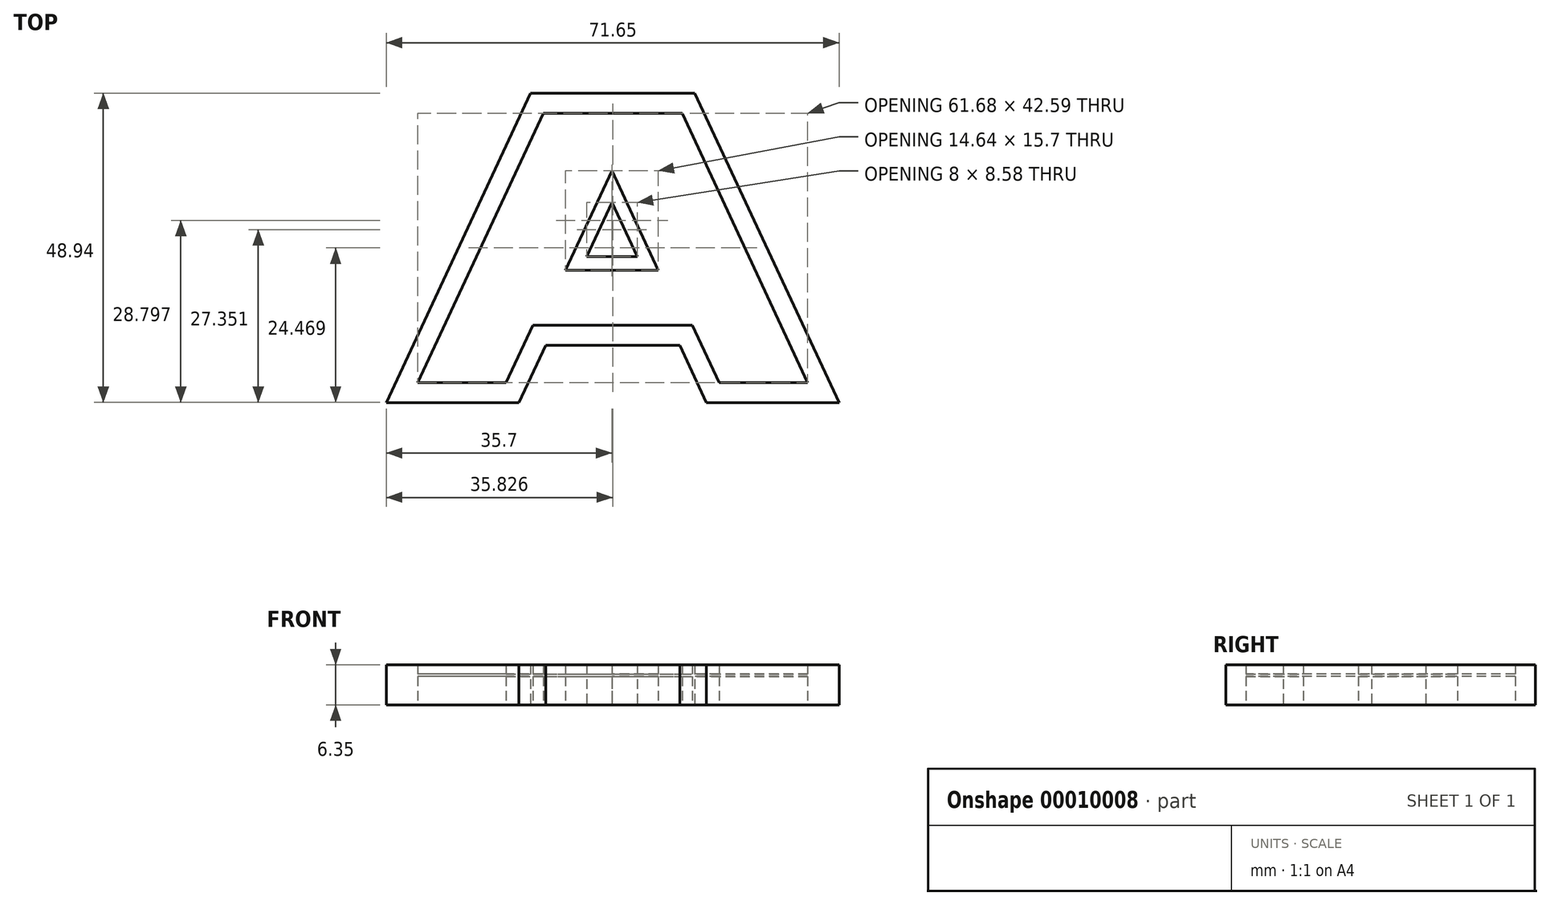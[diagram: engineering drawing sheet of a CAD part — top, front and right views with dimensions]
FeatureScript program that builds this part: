
annotation { "Feature Type Name" : "Feature", "Feature Type Description" : "" }
export const myFeature = defineFeature(function(context is Context, id is Id, definition is map)
    precondition{}
    {
        {
            var Q0;
            Q0=qCreatedBy(makeId("Top.planeOp"),FACE);
            var sketch = newSketch(context, id + "F0", { "sketchPlane" : qUnion([Q0])});
            skLineSegment(sketch, "E0", {"start": v(-12.87, 17.3) * mm, "end": v(13.13, 17.3) * mm});
            skLineSegment(sketch, "E1", {"start": v(13.13, 17.3) * mm, "end": v(35.95, -31.64) * mm});
            skLineSegment(sketch, "E2", {"start": v(-12.87, 17.3) * mm, "end": v(-35.7, -31.64) * mm});
            skLineSegment(sketch, "E3", {"start": v(-14.7, -31.64) * mm, "end": v(-35.7, -31.64) * mm});
            skLineSegment(sketch, "E4", {"start": v(35.95, -31.64) * mm, "end": v(14.95, -31.64) * mm});
            skLineSegment(sketch, "E5", {"start": v(-14.7, -31.64) * mm, "end": v(-10.47, -22.58) * mm});
            skLineSegment(sketch, "E6", {"start": v(14.95, -31.64) * mm, "end": v(10.72, -22.58) * mm});
            skLineSegment(sketch, "E7", {"start": v(-10.47, -22.58) * mm, "end": v(10.72, -22.58) * mm});
            skLineSegment(sketch, "E8", {"start": v(-4, -8.58) * mm, "end": v(4, -8.58) * mm});
            skLineSegment(sketch, "E9", {"start": v(-4, -8.58) * mm, "end": v(0, 0) * mm});
            skLineSegment(sketch, "E10", {"start": v(4, -8.58) * mm, "end": v(0, 0) * mm});
            skLineSegment(sketch, "E11.0", {"start": v(-10.85, 14.12) * mm, "end": v(11.1, 14.12) * mm});
            skLineSegment(sketch, "E11.1", {"start": v(11.1, 14.12) * mm, "end": v(30.96, -28.47) * mm});
            skLineSegment(sketch, "E11.2", {"start": v(30.96, -28.47) * mm, "end": v(16.97, -28.47) * mm});
            skLineSegment(sketch, "E11.3", {"start": v(16.97, -28.47) * mm, "end": v(12.74, -19.4) * mm});
            skLineSegment(sketch, "E11.4", {"start": v(-12.5, -19.4) * mm, "end": v(12.74, -19.4) * mm});
            skLineSegment(sketch, "E11.5", {"start": v(-10.85, 14.12) * mm, "end": v(-30.71, -28.47) * mm});
            skLineSegment(sketch, "E11.6", {"start": v(-16.72, -28.47) * mm, "end": v(-12.5, -19.4) * mm});
            skLineSegment(sketch, "E11.7", {"start": v(-16.72, -28.47) * mm, "end": v(-30.71, -28.47) * mm});
            skLineSegment(sketch, "E12.0", {"start": v(-7.32, -10.7) * mm, "end": v(0, 5) * mm});
            skLineSegment(sketch, "E12.1", {"start": v(-7.32, -10.7) * mm, "end": v(7.32, -10.7) * mm});
            skLineSegment(sketch, "E12.2", {"start": v(7.32, -10.7) * mm, "end": v(0, 5) * mm});
            skSolve(sketch);
        }
        {
            var Q0;
            Q0=makeQuery(id+"F0.imprint","IMPRINT",FACE,{"disambiguationData":[TD([[makeQuery(id+"F0.imprint","IMPRINT",EDGE,{"derivedFrom":sQuery(id+"F0.wireOp",EDGE,"E11.0")}),-1.0]])]});
            extrude(context, id + "F1", {"entities" : qUnion([Q0]), "depth" : 4.9 * mm});
        }
        {
            var Q0;
            Q0=makeQuery(id+"F0.imprint","IMPRINT",FACE,{"disambiguationData":[TD([[makeQuery(id+"F0.imprint","IMPRINT",EDGE,{"derivedFrom":sQuery(id+"F0.wireOp",EDGE,"E8")}),-1.0]])]});
            extrude(context, id + "F2", {"entities" : qUnion([Q0]), "operationType" : NewBodyOperationType.ADD, "depth" : 6.35 * mm});
        }
        {
            var Q0;
            Q0 = qSketchRegion(id + "F0", true);
            var Q1;
            Q1=makeQuery(id+"F0.imprint","IMPRINT",FACE,{"disambiguationData":[TD([[makeQuery(id+"F0.imprint","IMPRINT",EDGE,{"derivedFrom":sQuery(id+"F0.wireOp",EDGE,"E0")}),-1.0]])]});
            extrude(context, id + "F3", {"entities" : qUnion([Q0, Q1]), "operationType" : NewBodyOperationType.ADD, "flatOperationType" : FlatOperationType.REMOVE, "depth" : 6.35 * mm, "offsetDistance" : 25 * mm, "domain" : OperationDomain.MODEL});
        }
        {
            var Q0;
            Q0=makeQuery(id+"F0.imprint","IMPRINT",FACE,{"disambiguationData":[TD([[makeQuery(id+"F0.imprint","IMPRINT",EDGE,{"derivedFrom":sQuery(id+"F0.wireOp",EDGE,"E11.0")}),-1.0]])]});
            extrude(context, id + "F4", {"entities" : qUnion([Q0]), "operationType" : NewBodyOperationType.REMOVE, "depth" : 4.5 * mm});
        }
    });
